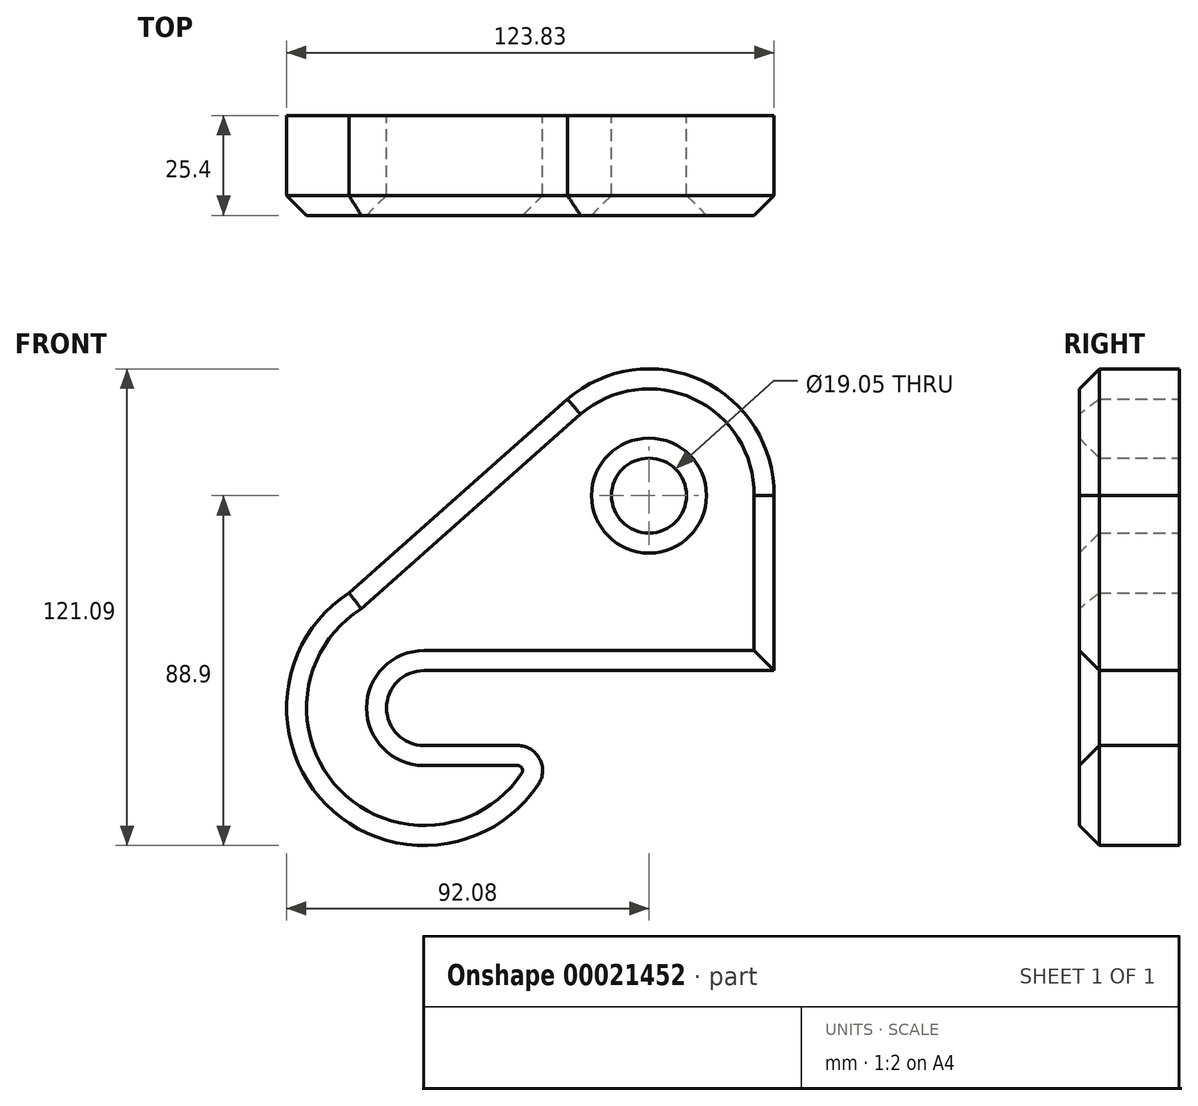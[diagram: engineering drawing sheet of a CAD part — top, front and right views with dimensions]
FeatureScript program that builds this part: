
annotation { "Feature Type Name" : "Feature", "Feature Type Description" : "" }
export const myFeature = defineFeature(function(context is Context, id is Id, definition is map)
    precondition{}
    {
        {
            var Q0;
            Q0=qCreatedBy(makeId("Front.planeOp"),FACE);
            var sketch = newSketch(context, id + "F0", { "sketchPlane" : qUnion([Q0])});
            skCircle(sketch, "E0", {"center": v(0, 0) * mm, "radius": 9.53 * mm});
            skLineSegment(sketch, "E1", {"start": v(0, 0) * mm, "end": v(31.75, 0) * mm});
            skLineSegment(sketch, "E2", {"start": v(31.75, 0) * mm, "end": v(31.75, -44.45) * mm});
            skLineSegment(sketch, "E3", {"start": v(31.75, -44.45) * mm, "end": v(-23.55, -44.45) * mm});
            skArc(sketch, "E4", {"start": v(-57.15, -44.45) * mm, "mid": v(-66.68, -53.98) * mm, "end": v(-57.15, -63.5) * mm});
            skLineSegment(sketch, "E5", {"start": v(-57.15, -63.5) * mm, "end": v(-33.4, -63.5) * mm});
            skLineSegment(sketch, "E6", {"start": v(-23.55, -44.45) * mm, "end": v(-23.55, -44.45) * mm});
            skPoint(sketch, "E7.visualSharp", {"position": v(-23.55, -63.5) * mm});
            skArc(sketch, "E7.filletArc", {"start": v(-28.11, -73.38) * mm, "mid": v(-27.8, -66.86) * mm, "end": v(-33.4, -63.5) * mm});
            skArc(sketch, "E8", {"start": v(31.75, 0) * mm, "mid": v(13.43, 29.21) * mm, "end": v(-20.72, 24.5) * mm});
            skLineSegment(sketch, "E9", {"start": v(-76.2, -24.7) * mm, "end": v(-76.2, -24.7) * mm});
            skLineSegment(sketch, "E10", {"start": v(-23.55, -44.45) * mm, "end": v(-57.15, -44.45) * mm});
            skArc(sketch, "E11", {"start": v(-76.2, -24.7) * mm, "mid": v(-82, -78.52) * mm, "end": v(-28.11, -73.38) * mm});
            skLineSegment(sketch, "E12", {"start": v(-76.2, -24.7) * mm, "end": v(-20.72, 24.5) * mm});
            skSolve(sketch);
        }
        {
            var Q0;
            Q0 = qSketchRegion(id + "F0", true);
            extrude(context, id + "F1", {"entities" : qUnion([Q0]), "depth" : 25.4 * mm});
        }
        {
            var Q0;
            Q0=makeQuery(id+"F1.opExtrude","CAP_FACE",FACE,{"disambiguationData":[OSD([sQuery(id+"F0.wireOp",EDGE,"E0"),sQuery(id+"F0.wireOp",EDGE,"E3"),sQuery(id+"F0.wireOp",EDGE,"E4"),sQuery(id+"F0.wireOp",EDGE,"E5"),sQuery(id+"F0.wireOp",EDGE,"E7.filletArc"),sQuery(id+"F0.wireOp",EDGE,"E8"),sQuery(id+"F0.wireOp",EDGE,"E10"),sQuery(id+"F0.wireOp",EDGE,"E11"),sQuery(id+"F0.wireOp",EDGE,"E2"),sQuery(id+"F0.wireOp",EDGE,"E12")])],"isStart":false});
            chamfer(context, id + "F2", {"entities" : qUnion([Q0]), "width" : 5.08 * mm, "tangentPropagation" : true});
        }
    });
